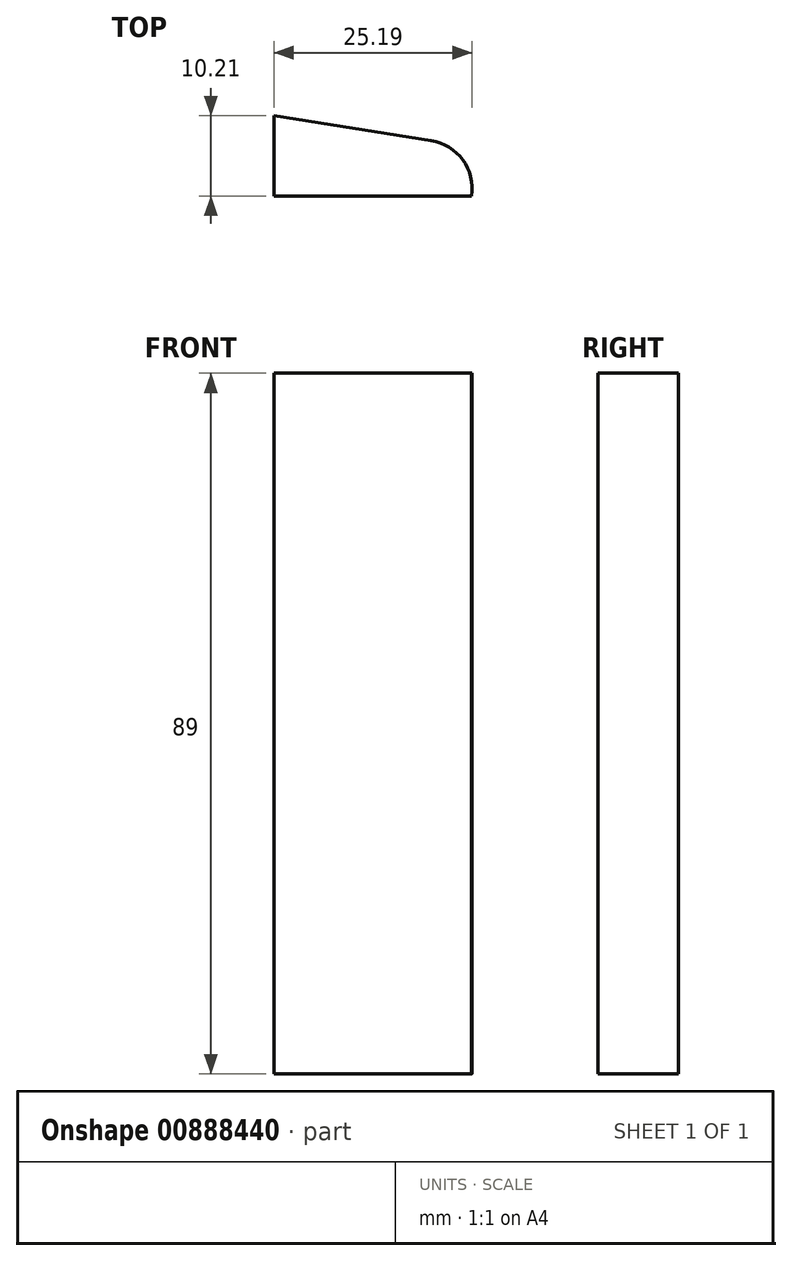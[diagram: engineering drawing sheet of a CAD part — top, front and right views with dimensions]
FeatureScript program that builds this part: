
annotation { "Feature Type Name" : "Feature", "Feature Type Description" : "" }
export const myFeature = defineFeature(function(context is Context, id is Id, definition is map)
    precondition{}
    {
        {
            var Q0;
            Q0=qCreatedBy(makeId("Top.planeOp"),FACE);
            var sketch = newSketch(context, id + "F0", { "sketchPlane" : qUnion([Q0])});
            skLineSegment(sketch, "E0", {"start": v(-25.12, 0) * mm, "end": v(-25.12, 10.2) * mm});
            skLineSegment(sketch, "E1", {"start": v(-25.12, 10.2) * mm, "end": v(-5.15, 7.06) * mm});
            skArc(sketch, "E2", {"start": v(0, 0) * mm, "mid": v(-1.12, 4.6) * mm, "end": v(-5.15, 7.06) * mm});
            skLineSegment(sketch, "E3", {"start": v(0, 0) * mm, "end": v(-25.12, 0) * mm});
            skSolve(sketch);
        }
        {
            var Q0;
            Q0 = qSketchRegion(id + "F0", true);
            extrude(context, id + "F1", {"entities" : qUnion([Q0]), "depth" : 89 * mm, "offsetDistance" : 25.4 * mm});
        }
    });
